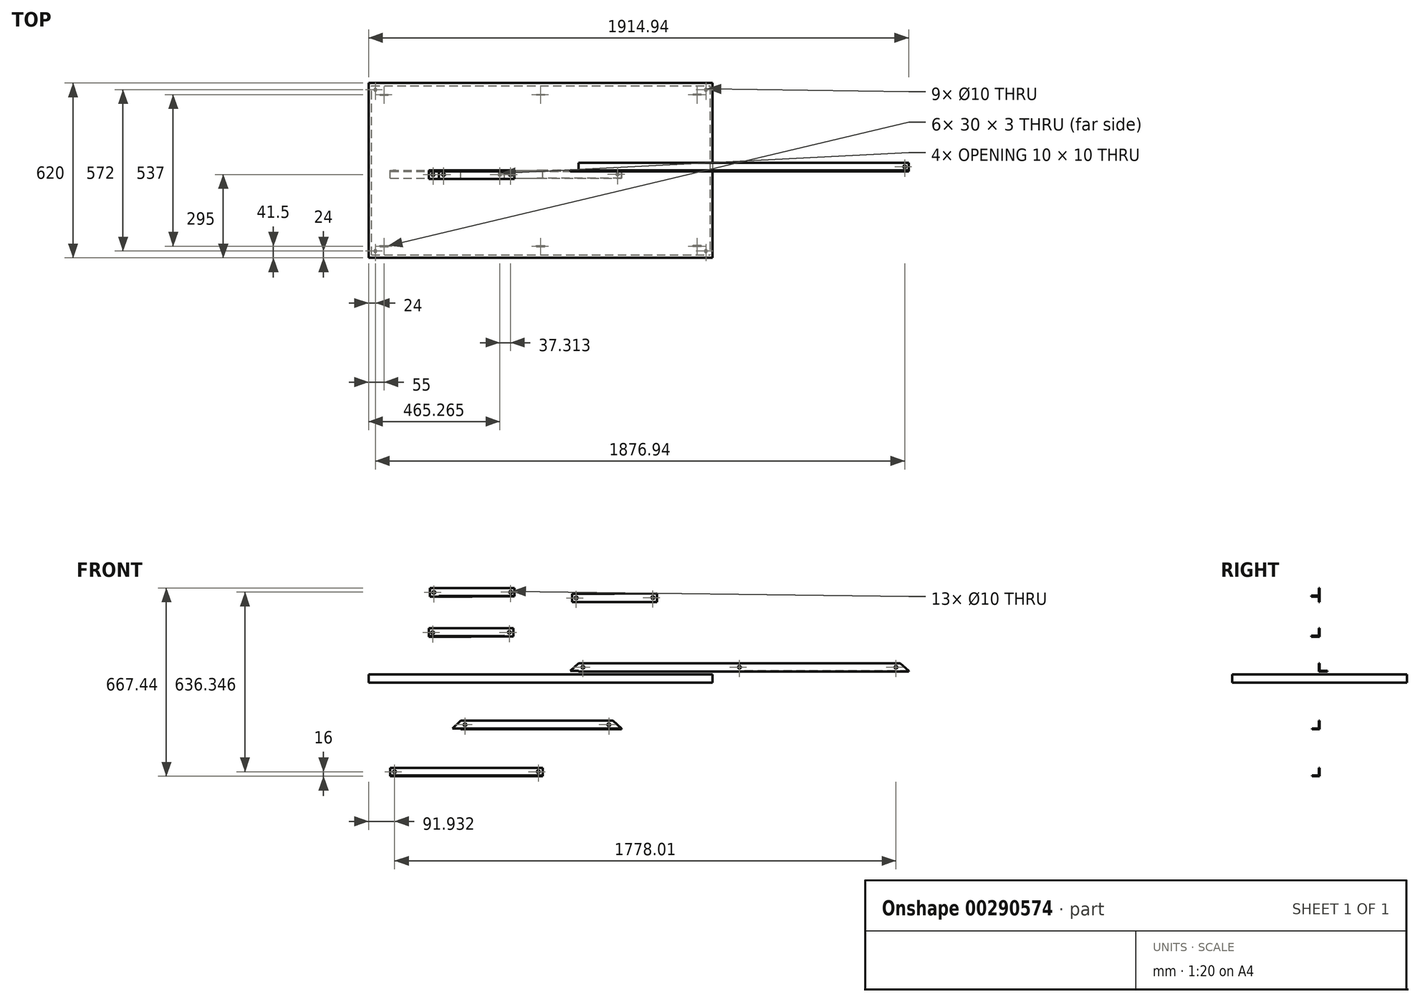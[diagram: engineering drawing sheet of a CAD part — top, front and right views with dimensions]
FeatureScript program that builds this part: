
annotation { "Feature Type Name" : "Feature", "Feature Type Description" : "" }
export const myFeature = defineFeature(function(context is Context, id is Id, definition is map)
    precondition{}
    {
        {
            var Q0;
            Q0=qCreatedBy(makeId("Front.planeOp"),FACE);
            var sketch = newSketch(context, id + "F0", { "sketchPlane" : qUnion([Q0])});
            skLineSegment(sketch, "E0.bottom", {"start": v(104.94, 39.43) * mm, "end": v(704.94, 39.43) * mm});
            skLineSegment(sketch, "E0.top", {"start": v(104.94, 42.43) * mm, "end": v(704.94, 42.43) * mm});
            skLineSegment(sketch, "E0.left", {"start": v(104.94, 39.43) * mm, "end": v(104.94, 42.43) * mm});
            skLineSegment(sketch, "E1.bottom", {"start": v(134.94, 69.43) * mm, "end": v(704.94, 69.43) * mm});
            skLineSegment(sketch, "E1.top", {"start": v(134.94, 42.43) * mm, "end": v(704.94, 42.43) * mm});
            skLineSegment(sketch, "E1.right", {"start": v(704.94, 69.43) * mm, "end": v(704.94, 42.43) * mm});
            skLineSegment(sketch, "E2", {"start": v(134.94, 69.43) * mm, "end": v(104.94, 42.43) * mm});
            skLineSegment(sketch, "E3", {"start": v(134.94, 42.43) * mm, "end": v(134.94, 39.43) * mm});
            skLineSegment(sketch, "E4", {"start": v(704.94, 42.43) * mm, "end": v(704.94, 39.43) * mm});
            skLineSegment(sketch, "E5.MirrorCS", {"start": v(1304.94, 42.43) * mm, "end": v(704.94, 42.43) * mm});
            skLineSegment(sketch, "E6.MirrorCS", {"start": v(1274.94, 69.43) * mm, "end": v(1304.94, 42.43) * mm});
            skLineSegment(sketch, "E7.MirrorCS", {"start": v(1274.94, 69.43) * mm, "end": v(704.94, 69.43) * mm});
            skLineSegment(sketch, "E8.MirrorCS", {"start": v(1274.94, 42.43) * mm, "end": v(1274.94, 39.43) * mm});
            skLineSegment(sketch, "E9.MirrorCS", {"start": v(1304.94, 39.43) * mm, "end": v(1304.94, 42.43) * mm});
            skLineSegment(sketch, "E10", {"start": v(704.94, 39.43) * mm, "end": v(1304.94, 39.43) * mm});
            skLineSegment(sketch, "E11", {"start": v(134.94, 69.43) * mm, "end": v(134.94, 42.43) * mm});
            skLineSegment(sketch, "E12", {"start": v(149.94, 69.43) * mm, "end": v(149.94, 42.43) * mm});
            skPoint(sketch, "E13", {"position": v(149.94, 55.43) * mm});
            skPoint(sketch, "E14", {"position": v(704.94, 55.43) * mm});
            skLineSegment(sketch, "E15.MirrorCS", {"start": v(1259.94, 69.43) * mm, "end": v(1259.94, 42.43) * mm});
            skPoint(sketch, "E16.MirrorP", {"position": v(1259.94, 55.43) * mm});
            skLineSegment(sketch, "E17.MirrorCS", {"start": v(1274.94, 69.43) * mm, "end": v(1274.94, 42.43) * mm});
            skCircle(sketch, "E18", {"center": v(704.94, 55.43) * mm, "radius": 5 * mm});
            skCircle(sketch, "E19", {"center": v(149.94, 55.43) * mm, "radius": 5 * mm});
            skCircle(sketch, "E20.MirrorC", {"center": v(1259.94, 55.43) * mm, "radius": 5 * mm});
            skLineSegment(sketch, "E21.bottom", {"start": v(-313.14, -164.51) * mm, "end": v(-13.14, -164.51) * mm});
            skLineSegment(sketch, "E21.top", {"start": v(-313.14, -161.51) * mm, "end": v(-13.14, -161.51) * mm});
            skLineSegment(sketch, "E21.left", {"start": v(-313.14, -164.51) * mm, "end": v(-313.14, -161.51) * mm});
            skLineSegment(sketch, "E22.bottom", {"start": v(-283.14, -134.51) * mm, "end": v(-13.14, -134.51) * mm});
            skLineSegment(sketch, "E22.top", {"start": v(-283.14, -161.51) * mm, "end": v(-13.14, -161.51) * mm});
            skLineSegment(sketch, "E22.right", {"start": v(-13.14, -134.51) * mm, "end": v(-13.14, -161.51) * mm});
            skLineSegment(sketch, "E23", {"start": v(-283.14, -134.51) * mm, "end": v(-313.14, -161.51) * mm});
            skLineSegment(sketch, "E24", {"start": v(-283.14, -161.51) * mm, "end": v(-283.14, -164.51) * mm});
            skLineSegment(sketch, "E25", {"start": v(-13.14, -161.51) * mm, "end": v(-13.14, -164.51) * mm});
            skLineSegment(sketch, "E26.MirrorCS", {"start": v(286.86, -161.51) * mm, "end": v(-13.14, -161.51) * mm});
            skLineSegment(sketch, "E27.MirrorCS", {"start": v(256.86, -134.51) * mm, "end": v(286.86, -161.51) * mm});
            skLineSegment(sketch, "E28.MirrorCS", {"start": v(256.86, -134.51) * mm, "end": v(-13.14, -134.51) * mm});
            skLineSegment(sketch, "E29.MirrorCS", {"start": v(256.86, -161.51) * mm, "end": v(256.86, -164.51) * mm});
            skLineSegment(sketch, "E30.MirrorCS", {"start": v(286.86, -164.51) * mm, "end": v(286.86, -161.51) * mm});
            skLineSegment(sketch, "E31", {"start": v(-13.14, -164.51) * mm, "end": v(286.86, -164.51) * mm});
            skLineSegment(sketch, "E32", {"start": v(-283.14, -134.51) * mm, "end": v(-283.14, -161.51) * mm});
            skLineSegment(sketch, "E33", {"start": v(-268.14, -134.51) * mm, "end": v(-268.14, -161.51) * mm});
            skPoint(sketch, "E34", {"position": v(-268.14, -148.51) * mm});
            skPoint(sketch, "E35", {"position": v(-13.14, -148.51) * mm});
            skLineSegment(sketch, "E36.MirrorCS", {"start": v(241.86, -134.51) * mm, "end": v(241.86, -161.51) * mm});
            skPoint(sketch, "E37.MirrorP", {"position": v(241.86, -148.51) * mm});
            skLineSegment(sketch, "E38.MirrorCS", {"start": v(256.86, -134.51) * mm, "end": v(256.86, -161.51) * mm});
            skCircle(sketch, "E39", {"center": v(-268.14, -148.51) * mm, "radius": 5 * mm});
            skCircle(sketch, "E40.MirrorC", {"center": v(241.86, -148.51) * mm, "radius": 5 * mm});
            skLineSegment(sketch, "E41.bottom", {"start": v(-396.7, 163.02) * mm, "end": v(-246.72, 163.02) * mm});
            skLineSegment(sketch, "E41.top", {"start": v(-396.7, 166.02) * mm, "end": v(-246.72, 166.02) * mm});
            skLineSegment(sketch, "E42.bottom", {"start": v(-396.9, 193.02) * mm, "end": v(-246.81, 193.02) * mm});
            skLineSegment(sketch, "E42.right", {"start": v(-246.81, 193.02) * mm, "end": v(-246.72, 166.02) * mm});
            skLineSegment(sketch, "E43", {"start": v(-396.7, 166.02) * mm, "end": v(-396.7, 163.02) * mm});
            skLineSegment(sketch, "E44", {"start": v(-246.72, 166.02) * mm, "end": v(-246.72, 163.02) * mm});
            skLineSegment(sketch, "E45.MirrorCS", {"start": v(-96.74, 167.05) * mm, "end": v(-246.72, 166.02) * mm});
            skLineSegment(sketch, "E46.MirrorCS", {"start": v(-96.74, 194.05) * mm, "end": v(-246.81, 193.02) * mm});
            skLineSegment(sketch, "E47.MirrorCS", {"start": v(-96.74, 167.05) * mm, "end": v(-96.71, 164.05) * mm});
            skLineSegment(sketch, "E48", {"start": v(-246.72, 163.02) * mm, "end": v(-96.71, 164.05) * mm});
            skLineSegment(sketch, "E49", {"start": v(-396.9, 193.02) * mm, "end": v(-396.7, 166.02) * mm});
            skLineSegment(sketch, "E50.MirrorCS", {"start": v(-96.74, 194.05) * mm, "end": v(-96.74, 167.05) * mm});
            skCircle(sketch, "E51", {"center": v(-382.8, 178.02) * mm, "radius": 5 * mm});
            skPoint(sketch, "E52.MirrorCS.start.orphan", {"position": v(-96.74, 194.05) * mm});
            skCircle(sketch, "E53.MirrorC", {"center": v(-110.74, 178.95) * mm, "radius": 5 * mm});
            skLineSegment(sketch, "E54.bottom", {"start": v(-533.07, -331.09) * mm, "end": v(-263.07, -331.09) * mm});
            skLineSegment(sketch, "E54.top", {"start": v(-533.07, -328.09) * mm, "end": v(-263.07, -328.09) * mm});
            skLineSegment(sketch, "E55.bottom", {"start": v(-533.07, -301.09) * mm, "end": v(-263.07, -301.09) * mm});
            skLineSegment(sketch, "E55.right", {"start": v(-263.07, -301.09) * mm, "end": v(-263.07, -328.09) * mm});
            skLineSegment(sketch, "E56", {"start": v(-533.07, -328.09) * mm, "end": v(-533.07, -331.09) * mm});
            skLineSegment(sketch, "E57", {"start": v(-263.07, -328.09) * mm, "end": v(-263.07, -331.09) * mm});
            skLineSegment(sketch, "E58.MirrorCS", {"start": v(6.93, -328.09) * mm, "end": v(-263.07, -328.09) * mm});
            skLineSegment(sketch, "E59.MirrorCS", {"start": v(6.93, -301.09) * mm, "end": v(-263.07, -301.09) * mm});
            skLineSegment(sketch, "E60.MirrorCS", {"start": v(6.93, -328.09) * mm, "end": v(6.93, -331.09) * mm});
            skLineSegment(sketch, "E61", {"start": v(-263.07, -331.09) * mm, "end": v(6.93, -331.09) * mm});
            skLineSegment(sketch, "E62", {"start": v(-533.07, -301.09) * mm, "end": v(-533.07, -328.09) * mm});
            skLineSegment(sketch, "E63", {"start": v(-518.07, -301.09) * mm, "end": v(-518.07, -328.09) * mm});
            skPoint(sketch, "E64", {"position": v(-518.07, -315.09) * mm});
            skPoint(sketch, "E65", {"position": v(-263.07, -315.09) * mm});
            skLineSegment(sketch, "E66.MirrorCS", {"start": v(-8.07, -301.09) * mm, "end": v(-8.07, -328.09) * mm});
            skPoint(sketch, "E67.MirrorP", {"position": v(-8.07, -315.09) * mm});
            skLineSegment(sketch, "E68.MirrorCS", {"start": v(6.93, -301.09) * mm, "end": v(6.93, -328.09) * mm});
            skCircle(sketch, "E69", {"center": v(-518.07, -315.09) * mm, "radius": 5 * mm});
            skCircle(sketch, "E70.MirrorC", {"center": v(-8.07, -315.09) * mm, "radius": 5 * mm});
            skLineSegment(sketch, "E71.bottom", {"start": v(112, 285.9) * mm, "end": v(261.99, 285.9) * mm});
            skLineSegment(sketch, "E72.bottom", {"start": v(111.81, 315.9) * mm, "end": v(261.9, 315.9) * mm});
            skLineSegment(sketch, "E73", {"start": v(112, 288.9) * mm, "end": v(112, 285.9) * mm});
            skLineSegment(sketch, "E74", {"start": v(261.99, 288.9) * mm, "end": v(261.99, 285.9) * mm});
            skLineSegment(sketch, "E75.MirrorCS", {"start": v(411.97, 316.93) * mm, "end": v(261.9, 315.9) * mm});
            skLineSegment(sketch, "E76.MirrorCS", {"start": v(411.97, 289.93) * mm, "end": v(412, 286.93) * mm});
            skLineSegment(sketch, "E77", {"start": v(261.99, 285.9) * mm, "end": v(412, 286.93) * mm});
            skLineSegment(sketch, "E78", {"start": v(111.81, 315.9) * mm, "end": v(112, 288.9) * mm});
            skLineSegment(sketch, "E79.MirrorCS", {"start": v(411.97, 316.93) * mm, "end": v(411.97, 289.93) * mm});
            skCircle(sketch, "E80", {"center": v(125.92, 300.9) * mm, "radius": 5 * mm});
            skPoint(sketch, "E81.MirrorCS.start.orphan", {"position": v(411.97, 316.93) * mm});
            skCircle(sketch, "E82.MirrorC", {"center": v(397.97, 301.84) * mm, "radius": 5 * mm});
            skLineSegment(sketch, "E83.bottom", {"start": v(-392.4, 305.32) * mm, "end": v(-242.4, 305.32) * mm});
            skLineSegment(sketch, "E83.top", {"start": v(-392.4, 308.32) * mm, "end": v(-242.4, 308.32) * mm});
            skLineSegment(sketch, "E84.bottom", {"start": v(-392.58, 335.32) * mm, "end": v(-242.5, 335.32) * mm});
            skLineSegment(sketch, "E84.right", {"start": v(-242.5, 335.32) * mm, "end": v(-242.4, 308.32) * mm});
            skLineSegment(sketch, "E85", {"start": v(-392.4, 308.32) * mm, "end": v(-392.4, 305.32) * mm});
            skLineSegment(sketch, "E86", {"start": v(-242.4, 308.32) * mm, "end": v(-242.4, 305.32) * mm});
            skLineSegment(sketch, "E87.MirrorCS", {"start": v(-92.42, 309.35) * mm, "end": v(-242.4, 308.32) * mm});
            skLineSegment(sketch, "E88.MirrorCS", {"start": v(-92.42, 336.35) * mm, "end": v(-242.5, 335.32) * mm});
            skLineSegment(sketch, "E89.MirrorCS", {"start": v(-92.42, 309.35) * mm, "end": v(-92.4, 306.35) * mm});
            skLineSegment(sketch, "E90", {"start": v(-242.4, 305.32) * mm, "end": v(-92.4, 306.35) * mm});
            skLineSegment(sketch, "E91", {"start": v(-392.58, 335.32) * mm, "end": v(-392.4, 308.32) * mm});
            skLineSegment(sketch, "E92.MirrorCS", {"start": v(-92.42, 336.35) * mm, "end": v(-92.42, 309.35) * mm});
            skCircle(sketch, "E93", {"center": v(-378.48, 320.32) * mm, "radius": 5 * mm});
            skPoint(sketch, "E94.MirrorCS.start.orphan", {"position": v(-92.42, 336.35) * mm});
            skCircle(sketch, "E95.MirrorC", {"center": v(-106.42, 321.26) * mm, "radius": 5 * mm});
            skLineSegment(sketch, "E96", {"start": v(-360.4, 308.32) * mm, "end": v(-360.4, 305.32) * mm});
            skLineSegment(sketch, "E97", {"start": v(-128.74, 166.83) * mm, "end": v(-128.71, 163.83) * mm});
            skSolve(sketch);
        }
        {
            var Q0;
            Q0=makeQuery(id+"F0.imprint","IMPRINT",FACE,{"disambiguationData":[TD([[makeQuery(id+"F0.imprint","IMPRINT",EDGE,{"derivedFrom":sQuery(id+"F0.wireOp",EDGE,"E1.top")}),-1.0]])]});
            var Q1;
            Q1=makeQuery(id+"F0.imprint","IMPRINT",FACE,{"disambiguationData":[TD([[makeQuery(id+"F0.imprint","IMPRINT",EDGE,{"derivedFrom":sQuery(id+"F0.wireOp",EDGE,"E0.top")}),-1.0]])]});
            var Q2;
            {var subQ0=sQuery(id+"F0.wireOp",EDGE,"E4");Q2=makeQuery(id+"F0.imprint","IMPRINT",FACE,{"disambiguationData":[TD([[makeQuery(id+"F0.imprint","IMPRINT",EDGE,{"derivedFrom":subQ0}),1.0]])]});}
            var Q3;
            {var subQ2=sQuery(id+"F0.wireOp",EDGE,"E8.MirrorCS");Q3=makeQuery(id+"F0.imprint","IMPRINT",FACE,{"disambiguationData":[TD([[makeQuery(id+"F0.imprint","IMPRINT",EDGE,{"derivedFrom":subQ2}),1.0]])]});}
            extrude(context, id + "F1", {"entities" : qUnion([Q0, Q1, Q2, Q3]), "oppositeDirection" : true, "depth" : 27 * mm});
        }
        {
            var Q0;
            Q0=makeQuery(id+"F0.imprint","IMPRINT",FACE,{"disambiguationData":[TD([[makeQuery(id+"F0.imprint","IMPRINT",EDGE,{"derivedFrom":sQuery(id+"F0.wireOp",EDGE,"E0.top")}),-1.0]])]});
            var Q1;
            Q1=makeQuery(id+"F0.imprint","IMPRINT",FACE,{"disambiguationData":[TD([[makeQuery(id+"F0.imprint","IMPRINT",EDGE,{"derivedFrom":sQuery(id+"F0.wireOp",EDGE,"E0.top")}),1.0]])]});
            var Q2;
            {var subQ0=sQuery(id+"F0.wireOp",EDGE,"E6.MirrorCS");Q2=makeQuery(id+"F0.imprint","IMPRINT",FACE,{"disambiguationData":[TD([[makeQuery(id+"F0.imprint","IMPRINT",EDGE,{"derivedFrom":subQ0}),-1.0]])]});}
            var Q3;
            {var subQ2=sQuery(id+"F0.wireOp",EDGE,"E8.MirrorCS");Q3=makeQuery(id+"F0.imprint","IMPRINT",FACE,{"disambiguationData":[TD([[makeQuery(id+"F0.imprint","IMPRINT",EDGE,{"derivedFrom":subQ2}),1.0]])]});}
            var Q4;
            Q4=makeQuery(id+"F0.imprint","IMPRINT",FACE,{"disambiguationData":[TD([[makeQuery(id+"F0.imprint","IMPRINT",EDGE,{"derivedFrom":sQuery(id+"F0.wireOp",EDGE,"E21.top")}),-1.0]])]});
            var Q5;
            Q5=makeQuery(id+"F0.imprint","IMPRINT",FACE,{"disambiguationData":[TD([[makeQuery(id+"F0.imprint","IMPRINT",EDGE,{"derivedFrom":sQuery(id+"F0.wireOp",EDGE,"E21.top")}),1.0]])]});
            var Q6;
            {var subQ0=sQuery(id+"F0.wireOp",EDGE,"E27.MirrorCS");Q6=makeQuery(id+"F0.imprint","IMPRINT",FACE,{"disambiguationData":[TD([[makeQuery(id+"F0.imprint","IMPRINT",EDGE,{"derivedFrom":subQ0}),-1.0]])]});}
            var Q7;
            {var subQ2=sQuery(id+"F0.wireOp",EDGE,"E29.MirrorCS");Q7=makeQuery(id+"F0.imprint","IMPRINT",FACE,{"disambiguationData":[TD([[makeQuery(id+"F0.imprint","IMPRINT",EDGE,{"derivedFrom":subQ2}),1.0]])]});}
            var Q8;
            Q8=makeQuery(id+"F0.imprint","IMPRINT",FACE,{"disambiguationData":[TD([[makeQuery(id+"F0.imprint","IMPRINT",EDGE,{"derivedFrom":sQuery(id+"F0.wireOp",EDGE,"E41.bottom")}),1.0]])]});
            var Q9;
            Q9=makeQuery(id+"F0.imprint","IMPRINT",FACE,{"disambiguationData":[TD([[makeQuery(id+"F0.imprint","IMPRINT",EDGE,{"derivedFrom":sQuery(id+"F0.wireOp",EDGE,"E44")}),1.0]])]});
            var Q10;
            Q10=makeQuery(id+"F0.imprint","IMPRINT",FACE,{"disambiguationData":[TD([[makeQuery(id+"F0.imprint","IMPRINT",EDGE,{"derivedFrom":sQuery(id+"F0.wireOp",EDGE,"E71.bottom")}),1.0]])]});
            var Q11;
            Q11=makeQuery(id+"F0.imprint","IMPRINT",FACE,{"disambiguationData":[TD([[makeQuery(id+"F0.imprint","IMPRINT",EDGE,{"derivedFrom":sQuery(id+"F0.wireOp",EDGE,"E42.bottom")}),-1.0]])]});
            var Q12;
            Q12=makeQuery(id+"F0.imprint","IMPRINT",FACE,{"disambiguationData":[TD([[makeQuery(id+"F0.imprint","IMPRINT",EDGE,{"derivedFrom":sQuery(id+"F0.wireOp",EDGE,"E42.right")}),1.0]])]});
            var Q13;
            Q13=makeQuery(id+"F0.imprint","IMPRINT",FACE,{"disambiguationData":[TD([[makeQuery(id+"F0.imprint","IMPRINT",EDGE,{"derivedFrom":sQuery(id+"F0.wireOp",EDGE,"E54.bottom")}),1.0]])]});
            var Q14;
            {var subQ5=sQuery(id+"F0.wireOp",EDGE,"E62");Q14=makeQuery(id+"F0.imprint","IMPRINT",FACE,{"disambiguationData":[TD([[makeQuery(id+"F0.imprint","IMPRINT",EDGE,{"derivedFrom":subQ5}),1.0]])]});}
            var Q15;
            {var subQ1=sQuery(id+"F0.wireOp",EDGE,"E57");Q15=makeQuery(id+"F0.imprint","IMPRINT",FACE,{"disambiguationData":[TD([[makeQuery(id+"F0.imprint","IMPRINT",EDGE,{"derivedFrom":subQ1}),1.0]])]});}
            var Q16;
            {var subQ5=sQuery(id+"F0.wireOp",EDGE,"E68.MirrorCS");Q16=makeQuery(id+"F0.imprint","IMPRINT",FACE,{"disambiguationData":[TD([[makeQuery(id+"F0.imprint","IMPRINT",EDGE,{"derivedFrom":subQ5}),-1.0]])]});}
            var Q17;
            {var subQ0=sQuery(id+"F0.wireOp",EDGE,"E3");Q17=makeQuery(id+"F0.imprint","IMPRINT",FACE,{"disambiguationData":[TD([[makeQuery(id+"F0.imprint","IMPRINT",EDGE,{"derivedFrom":subQ0}),1.0]])]});}
            var Q18;
            {var subQ5=sQuery(id+"F0.wireOp",EDGE,"E11");Q18=makeQuery(id+"F0.imprint","IMPRINT",FACE,{"disambiguationData":[TD([[makeQuery(id+"F0.imprint","IMPRINT",EDGE,{"derivedFrom":subQ5}),1.0]])]});}
            var Q19;
            {var subQ1=sQuery(id+"F0.wireOp",EDGE,"E4");Q19=makeQuery(id+"F0.imprint","IMPRINT",FACE,{"disambiguationData":[TD([[makeQuery(id+"F0.imprint","IMPRINT",EDGE,{"derivedFrom":subQ1}),1.0]])]});}
            var Q20;
            {var subQ5=sQuery(id+"F0.wireOp",EDGE,"E17.MirrorCS");Q20=makeQuery(id+"F0.imprint","IMPRINT",FACE,{"disambiguationData":[TD([[makeQuery(id+"F0.imprint","IMPRINT",EDGE,{"derivedFrom":subQ5}),-1.0]])]});}
            var Q21;
            {var subQ0=sQuery(id+"F0.wireOp",EDGE,"E24");Q21=makeQuery(id+"F0.imprint","IMPRINT",FACE,{"disambiguationData":[TD([[makeQuery(id+"F0.imprint","IMPRINT",EDGE,{"derivedFrom":subQ0}),1.0]])]});}
            var Q22;
            {var subQ5=sQuery(id+"F0.wireOp",EDGE,"E32");Q22=makeQuery(id+"F0.imprint","IMPRINT",FACE,{"disambiguationData":[TD([[makeQuery(id+"F0.imprint","IMPRINT",EDGE,{"derivedFrom":subQ5}),1.0]])]});}
            var Q23;
            {var subQ1=sQuery(id+"F0.wireOp",EDGE,"E25");Q23=makeQuery(id+"F0.imprint","IMPRINT",FACE,{"disambiguationData":[TD([[makeQuery(id+"F0.imprint","IMPRINT",EDGE,{"derivedFrom":subQ1}),1.0]])]});}
            var Q24;
            {var subQ5=sQuery(id+"F0.wireOp",EDGE,"E38.MirrorCS");Q24=makeQuery(id+"F0.imprint","IMPRINT",FACE,{"disambiguationData":[TD([[makeQuery(id+"F0.imprint","IMPRINT",EDGE,{"derivedFrom":subQ5}),-1.0]])]});}
            var Q25;
            {var subQ1=sQuery(id+"F0.wireOp",EDGE,"E1.bottom");var subQ7=sQuery(id+"F0.wireOp",EDGE,"E12");var subQ10=makeQuery(id+"F0.imprint","INTERSECT",VERTEX,{"derivedFrom":[subQ1,subQ7]});Q25=makeQuery(id+"F0.imprint","IMPRINT",FACE,{"disambiguationData":[TD([[makeQuery(id+"F0.imprint","IMPRINT",EDGE,{"disambiguationData":[TD([[subQ10,-1.0]])],"derivedFrom":subQ7}),1.0]])]});}
            var Q26;
            {var subQ0=sQuery(id+"F0.wireOp",EDGE,"E7.MirrorCS");var subQ3=sQuery(id+"F0.wireOp",EDGE,"E15.MirrorCS");var subQ4=makeQuery(id+"F0.imprint","INTERSECT",VERTEX,{"derivedFrom":[subQ0,subQ3]});Q26=makeQuery(id+"F0.imprint","IMPRINT",FACE,{"disambiguationData":[TD([[makeQuery(id+"F0.imprint","IMPRINT",EDGE,{"disambiguationData":[TD([[subQ4,-1.0]])],"derivedFrom":subQ3}),-1.0]])]});}
            var Q27;
            {var subQ1=sQuery(id+"F0.wireOp",EDGE,"E22.bottom");var subQ7=sQuery(id+"F0.wireOp",EDGE,"E33");var subQ10=makeQuery(id+"F0.imprint","INTERSECT",VERTEX,{"derivedFrom":[subQ1,subQ7]});Q27=makeQuery(id+"F0.imprint","IMPRINT",FACE,{"disambiguationData":[TD([[makeQuery(id+"F0.imprint","IMPRINT",EDGE,{"disambiguationData":[TD([[subQ10,-1.0]])],"derivedFrom":subQ7}),1.0]])]});}
            var Q28;
            {var subQ1=sQuery(id+"F0.wireOp",EDGE,"E55.bottom");var subQ6=sQuery(id+"F0.wireOp",EDGE,"E63");var subQ13=makeQuery(id+"F0.imprint","INTERSECT",VERTEX,{"derivedFrom":[subQ1,subQ6]});Q28=makeQuery(id+"F0.imprint","IMPRINT",FACE,{"disambiguationData":[TD([[makeQuery(id+"F0.imprint","IMPRINT",EDGE,{"disambiguationData":[TD([[subQ13,-1.0]])],"derivedFrom":subQ6}),1.0]])]});}
            var Q29;
            {var subQ0=sQuery(id+"F0.wireOp",EDGE,"E59.MirrorCS");var subQ3=sQuery(id+"F0.wireOp",EDGE,"E66.MirrorCS");var subQ4=makeQuery(id+"F0.imprint","INTERSECT",VERTEX,{"derivedFrom":[subQ0,subQ3]});Q29=makeQuery(id+"F0.imprint","IMPRINT",FACE,{"disambiguationData":[TD([[makeQuery(id+"F0.imprint","IMPRINT",EDGE,{"disambiguationData":[TD([[subQ4,-1.0]])],"derivedFrom":subQ3}),-1.0]])]});}
            var Q30;
            {var subQ0=sQuery(id+"F0.wireOp",EDGE,"a2b34186-37aa-447c-9af8-30680829358e");var subQ1=sQuery(id+"F0.wireOp",EDGE,"E22.right");var subQ2=makeQuery(id+"F0.imprint","INTERSECT",VERTEX,{"disambiguationData":[OD(0.0)],"derivedFrom":[subQ1,subQ0]});Q30=makeQuery(id+"F0.imprint","IMPRINT",FACE,{"disambiguationData":[TD([[makeQuery(id+"F0.imprint","IMPRINT",EDGE,{"disambiguationData":[TD([[subQ2,-1.0]])],"derivedFrom":subQ1}),1.0]])]});}
            var Q31;
            {var subQ0=sQuery(id+"F0.wireOp",EDGE,"a2b34186-37aa-447c-9af8-30680829358e");var subQ1=sQuery(id+"F0.wireOp",EDGE,"E22.right");var subQ2=makeQuery(id+"F0.imprint","INTERSECT",VERTEX,{"disambiguationData":[OD(0.0)],"derivedFrom":[subQ1,subQ0]});Q31=makeQuery(id+"F0.imprint","IMPRINT",FACE,{"disambiguationData":[TD([[makeQuery(id+"F0.imprint","IMPRINT",EDGE,{"disambiguationData":[TD([[subQ2,-1.0]])],"derivedFrom":subQ1}),-1.0]])]});}
            var Q32;
            Q32=makeQuery(id+"F0.imprint","IMPRINT",FACE,{"disambiguationData":[TD([[makeQuery(id+"F0.imprint","IMPRINT",EDGE,{"derivedFrom":sQuery(id+"F0.wireOp",EDGE,"E84.bottom")}),-1.0]])]});
            var Q33;
            Q33=makeQuery(id+"F0.imprint","IMPRINT",FACE,{"disambiguationData":[TD([[makeQuery(id+"F0.imprint","IMPRINT",EDGE,{"derivedFrom":sQuery(id+"F0.wireOp",EDGE,"E84.right")}),1.0]])]});
            var Q34;
            Q34=makeQuery(id+"F0.imprint","IMPRINT",FACE,{"disambiguationData":[TD([[makeQuery(id+"F0.imprint","IMPRINT",EDGE,{"derivedFrom":sQuery(id+"F0.wireOp",EDGE,"E83.bottom")}),1.0]])]});
            var Q35;
            Q35=makeQuery(id+"F0.imprint","IMPRINT",FACE,{"disambiguationData":[TD([[makeQuery(id+"F0.imprint","IMPRINT",EDGE,{"derivedFrom":sQuery(id+"F0.wireOp",EDGE,"E86")}),1.0]])]});
            var Q36;
            {var subQ0=sQuery(id+"F0.wireOp",EDGE,"E47.MirrorCS");Q36=makeQuery(id+"F0.imprint","IMPRINT",FACE,{"disambiguationData":[TD([[makeQuery(id+"F0.imprint","IMPRINT",EDGE,{"derivedFrom":subQ0}),-1.0]])]});}
            extrude(context, id + "F2", {"entities" : qUnion([Q0, Q1, Q2, Q3, Q4, Q5, Q6, Q7, Q8, Q9, Q10, Q11, Q12, Q13, Q14, Q15, Q16, Q17, Q18, Q19, Q20, Q21, Q22, Q23, Q24, Q25, Q26, Q27, Q28, Q29, Q30, Q31, Q32, Q33, Q34, Q35, Q36]), "operationType" : NewBodyOperationType.ADD, "depth" : 3 * mm});
        }
        {
            var Q0;
            Q0=makeQuery(id+"F1.opExtrude","SWEPT_FACE",FACE,{"disambiguationData":[OSD([sQuery(id+"F0.wireOp",EDGE,"E0.top"),sQuery(id+"F0.wireOp",EDGE,"E1.top")])]});
            var sketch = newSketch(context, id + "F3", { "sketchPlane" : qUnion([Q0])});
            skLineSegment(sketch, "E98", {"start": v(118.94, 27) * mm, "end": v(118.94, 0) * mm});
            skPoint(sketch, "E99", {"position": v(118.94, 13) * mm});
            skCircle(sketch, "E100", {"center": v(118.94, 13) * mm, "radius": 5 * mm});
            skLineSegment(sketch, "E101.MirrorCS", {"start": v(1290.94, 27) * mm, "end": v(1290.94, 0) * mm});
            skPoint(sketch, "E102.MirrorP", {"position": v(1290.94, 13) * mm});
            skCircle(sketch, "E103.MirrorC", {"center": v(1290.94, 13) * mm, "radius": 5 * mm});
            skLineSegment(sketch, "E104", {"start": v(104.94, 27) * mm, "end": v(104.94, 0) * mm});
            skSolve(sketch);
        }
        {
            var Q0;
            Q0 = qSketchRegion(id + "F3", true);
            extrude(context, id + "F4", {"entities" : qUnion([Q0]), "operationType" : NewBodyOperationType.REMOVE, "endBound" : BoundingType.THROUGH_ALL, "oppositeDirection" : true, "depth" : 25 * mm});
        }
        {
            var Q0;
            Q0=qCreatedBy(makeId("Top.planeOp"),FACE);
            var sketch = newSketch(context, id + "F5", { "sketchPlane" : qUnion([Q0])});
            skLineSegment(sketch, "E105.bottom", {"start": v(-600, 270) * mm, "end": v(0, 270) * mm});
            skLineSegment(sketch, "E105.top", {"start": v(-600, 300) * mm, "end": v(0, 300) * mm});
            skLineSegment(sketch, "E105.left", {"start": v(-600, 270) * mm, "end": v(-600, 300) * mm});
            skLineSegment(sketch, "E105.right", {"start": v(0, 270) * mm, "end": v(0, 300) * mm});
            skLineSegment(sketch, "E106.bottom", {"start": v(-600, 300) * mm, "end": v(-570, 300) * mm});
            skLineSegment(sketch, "E106.top", {"start": v(-600, 0) * mm, "end": v(-570, 0) * mm});
            skLineSegment(sketch, "E106.left", {"start": v(-600, 300) * mm, "end": v(-600, 0) * mm});
            skLineSegment(sketch, "E106.right", {"start": v(-570, 300) * mm, "end": v(-570, 0) * mm});
            skLineSegment(sketch, "E107.bottom", {"start": v(-570, 270) * mm, "end": v(-540, 270) * mm});
            skLineSegment(sketch, "E107.top", {"start": v(-570, 267) * mm, "end": v(-540, 267) * mm});
            skLineSegment(sketch, "E107.left", {"start": v(-570, 270) * mm, "end": v(-570, 267) * mm});
            skLineSegment(sketch, "E107.right", {"start": v(-540, 270) * mm, "end": v(-540, 267) * mm});
            skLineSegment(sketch, "E108.bottom", {"start": v(-570, 267) * mm, "end": v(-567, 267) * mm});
            skLineSegment(sketch, "E108.left", {"start": v(-570, 267) * mm, "end": v(-570, 240) * mm});
            skLineSegment(sketch, "E109.bottom", {"start": v(-15, 270) * mm, "end": v(0, 270) * mm});
            skLineSegment(sketch, "E109.top", {"start": v(-15, 267) * mm, "end": v(0, 267) * mm});
            skLineSegment(sketch, "E109.left", {"start": v(-15, 270) * mm, "end": v(-15, 267) * mm});
            skLineSegment(sketch, "E109.right", {"start": v(0, 270) * mm, "end": v(0, 267) * mm});
            skLineSegment(sketch, "E110.MirrorCS", {"start": v(600, 300) * mm, "end": v(0, 300) * mm});
            skLineSegment(sketch, "E111.MirrorCS", {"start": v(600, 300) * mm, "end": v(600, 0) * mm});
            skLineSegment(sketch, "E112.MirrorCS", {"start": v(600, 270) * mm, "end": v(0, 270) * mm});
            skLineSegment(sketch, "E113.MirrorCS", {"start": v(570, 300) * mm, "end": v(570, 0) * mm});
            skLineSegment(sketch, "E114.MirrorCS", {"start": v(570, 267) * mm, "end": v(540, 267) * mm});
            skLineSegment(sketch, "E115.MirrorCS", {"start": v(540, 270) * mm, "end": v(540, 267) * mm});
            skLineSegment(sketch, "E116.MirrorCS", {"start": v(15, 267) * mm, "end": v(0, 267) * mm});
            skLineSegment(sketch, "E117.MirrorCS", {"start": v(15, 270) * mm, "end": v(15, 267) * mm});
            skLineSegment(sketch, "E118.MirrorCS", {"start": v(600, 0) * mm, "end": v(570, 0) * mm});
            skLineSegment(sketch, "E119.MirrorCS", {"start": v(0, -270) * mm, "end": v(0, -267) * mm});
            skLineSegment(sketch, "E120.MirrorCS", {"start": v(15, -267) * mm, "end": v(0, -267) * mm});
            skLineSegment(sketch, "E121.MirrorCS", {"start": v(-15, -267) * mm, "end": v(0, -267) * mm});
            skLineSegment(sketch, "E122.MirrorCS", {"start": v(-570, -267) * mm, "end": v(-567, -267) * mm});
            skLineSegment(sketch, "E123.MirrorCS", {"start": v(-570, -270) * mm, "end": v(-570, -267) * mm});
            skLineSegment(sketch, "E124.MirrorCS", {"start": v(-15, -270) * mm, "end": v(-15, -267) * mm});
            skLineSegment(sketch, "E125.MirrorCS", {"start": v(-15, -270) * mm, "end": v(0, -270) * mm});
            skLineSegment(sketch, "E126.MirrorCS", {"start": v(-570, -270) * mm, "end": v(-540, -270) * mm});
            skLineSegment(sketch, "E127.MirrorCS", {"start": v(0, -270) * mm, "end": v(0, -300) * mm});
            skLineSegment(sketch, "E128.MirrorCS", {"start": v(-570, -267) * mm, "end": v(-540, -267) * mm});
            skLineSegment(sketch, "E129.MirrorCS", {"start": v(-540, -270) * mm, "end": v(-540, -267) * mm});
            skLineSegment(sketch, "E130.MirrorCS", {"start": v(-570, -267) * mm, "end": v(-570, -240) * mm});
            skLineSegment(sketch, "E131.MirrorCS", {"start": v(-600, -270) * mm, "end": v(-600, -300) * mm});
            skLineSegment(sketch, "E132.MirrorCS", {"start": v(15, -270) * mm, "end": v(15, -267) * mm});
            skLineSegment(sketch, "E133.MirrorCS", {"start": v(540, -270) * mm, "end": v(540, -267) * mm});
            skLineSegment(sketch, "E134.MirrorCS", {"start": v(570, -267) * mm, "end": v(540, -267) * mm});
            skLineSegment(sketch, "E135.MirrorCS", {"start": v(-600, -300) * mm, "end": v(-570, -300) * mm});
            skLineSegment(sketch, "E136.MirrorCS", {"start": v(570, -300) * mm, "end": v(570, 0) * mm});
            skLineSegment(sketch, "E137.MirrorCS", {"start": v(600, -270) * mm, "end": v(0, -270) * mm});
            skLineSegment(sketch, "E138.MirrorCS", {"start": v(600, -300) * mm, "end": v(600, 0) * mm});
            skLineSegment(sketch, "E139.MirrorCS", {"start": v(600, -300) * mm, "end": v(0, -300) * mm});
            skLineSegment(sketch, "E140.MirrorCS", {"start": v(-570, -300) * mm, "end": v(-570, 0) * mm});
            skLineSegment(sketch, "E141.MirrorCS", {"start": v(-600, -270) * mm, "end": v(0, -270) * mm});
            skLineSegment(sketch, "E142.MirrorCS", {"start": v(-600, -300) * mm, "end": v(0, -300) * mm});
            skLineSegment(sketch, "E143.MirrorCS", {"start": v(-600, -300) * mm, "end": v(-600, 0) * mm});
            skCircle(sketch, "E144", {"center": v(-586, 286) * mm, "radius": 5 * mm});
            skCircle(sketch, "E145.MirrorC", {"center": v(586, 286) * mm, "radius": 5 * mm});
            skCircle(sketch, "E146.MirrorC", {"center": v(-586, -286) * mm, "radius": 5 * mm});
            skCircle(sketch, "E147.MirrorC", {"center": v(586, -286) * mm, "radius": 5 * mm});
            skSolve(sketch);
        }
        {
            var Q0;
            Q0=qCreatedBy(makeId("Front.planeOp"),FACE);
            var sketch = newSketch(context, id + "F6", { "sketchPlane" : qUnion([Q0])});
            skLineSegment(sketch, "E148.bottom", {"start": v(526.62, -156.75) * mm, "end": v(-539.74, -156.75) * mm});
            skLineSegment(sketch, "E148.top", {"start": v(526.62, 141.93) * mm, "end": v(-539.74, 141.93) * mm});
            skLineSegment(sketch, "E148.left", {"start": v(526.62, -156.75) * mm, "end": v(526.62, 141.93) * mm});
            skLineSegment(sketch, "E148.right", {"start": v(-539.74, -156.75) * mm, "end": v(-539.74, 141.93) * mm});
            skLineSegment(sketch, "E149.bottom", {"start": v(600, 170.75) * mm, "end": v(-600, 170.75) * mm});
            skLineSegment(sketch, "E149.top", {"start": v(600, 141.93) * mm, "end": v(-600, 141.93) * mm});
            skLineSegment(sketch, "E149.left", {"start": v(600, 170.75) * mm, "end": v(600, 141.93) * mm});
            skLineSegment(sketch, "E149.right", {"start": v(-600, 170.75) * mm, "end": v(-600, 141.93) * mm});
            skLineSegment(sketch, "E150.bottom", {"start": v(-505.68, 107.87) * mm, "end": v(500.42, 107.87) * mm});
            skLineSegment(sketch, "E150.top", {"start": v(-505.68, -127.93) * mm, "end": v(500.42, -127.93) * mm});
            skLineSegment(sketch, "E150.left", {"start": v(-505.68, 107.87) * mm, "end": v(-505.68, -127.93) * mm});
            skLineSegment(sketch, "E150.right", {"start": v(500.42, 107.87) * mm, "end": v(500.42, -127.93) * mm});
            skPoint(sketch, "E151.firstSnap0", {"position": v(-6.56, 141.93) * mm});
            skLineSegment(sketch, "E151.bottom", {"start": v(-6.56, 107.87) * mm, "end": v(26.2, 107.87) * mm});
            skLineSegment(sketch, "E151.top", {"start": v(-6.56, -127.93) * mm, "end": v(26.2, -127.93) * mm});
            skLineSegment(sketch, "E151.left", {"start": v(-6.56, 107.87) * mm, "end": v(-6.56, -127.93) * mm});
            skLineSegment(sketch, "E151.right", {"start": v(26.2, 107.87) * mm, "end": v(26.2, -127.93) * mm});
            skCircle(sketch, "E152", {"center": v(9.82, 130.43) * mm, "radius": 9.27 * mm});
            skPoint(sketch, "E152.centerSnap0", {"position": v(9.82, 107.87) * mm});
            skLineSegment(sketch, "E153.bottom", {"start": v(-472.12, 82.9) * mm, "end": v(-41.39, 82.9) * mm});
            skLineSegment(sketch, "E153.top", {"start": v(-472.12, -102.57) * mm, "end": v(-41.39, -102.57) * mm});
            skLineSegment(sketch, "E153.left", {"start": v(-472.12, 82.9) * mm, "end": v(-472.12, -102.57) * mm});
            skLineSegment(sketch, "E153.right", {"start": v(-41.39, 82.9) * mm, "end": v(-41.39, -102.57) * mm});
            skLineSegment(sketch, "E154.bottom", {"start": v(58.25, 78.3) * mm, "end": v(472.12, 78.3) * mm});
            skLineSegment(sketch, "E154.top", {"start": v(58.25, -102.57) * mm, "end": v(472.12, -102.57) * mm});
            skLineSegment(sketch, "E154.left", {"start": v(58.25, 78.3) * mm, "end": v(58.25, -102.57) * mm});
            skLineSegment(sketch, "E154.right", {"start": v(472.12, 78.3) * mm, "end": v(472.12, -102.57) * mm});
            skLineSegment(sketch, "E155", {"start": v(-539.74, 113.56) * mm, "end": v(-571.75, 141.93) * mm});
            skCircle(sketch, "E156", {"center": v(-505.68, -250.86) * mm, "radius": 79.3 * mm});
            skCircle(sketch, "E157", {"center": v(496.64, -247.32) * mm, "radius": 80.23 * mm});
            skPoint(sketch, "E158", {"position": v(-578.92, -144.72) * mm});
            skPoint(sketch, "E159", {"position": v(-448.01, -141.18) * mm});
            skPoint(sketch, "E160", {"position": v(500.42, -327.46) * mm});
            skPoint(sketch, "E161", {"position": v(496.64, -156.75) * mm});
            skCircle(sketch, "E162", {"center": v(-522.93, 130.55) * mm, "radius": 8.16 * mm});
            skSolve(sketch);
        }
        {
            var Q0;
            Q0=makeQuery(id+"F1.opExtrude","SWEPT_BODY",BODY,{"disambiguationData":[OSD([sQuery(id+"F0.wireOp",EDGE,"E0.bottom"),sQuery(id+"F0.wireOp",EDGE,"E0.top"),sQuery(id+"F0.wireOp",EDGE,"E0.left"),sQuery(id+"F0.wireOp",EDGE,"E1.top"),sQuery(id+"F0.wireOp",EDGE,"E5.MirrorCS"),sQuery(id+"F0.wireOp",EDGE,"E9.MirrorCS"),sQuery(id+"F0.wireOp",EDGE,"E10")])]});
            transform(context, id + "F7", {"entities" : qUnion([Q0]), "transformType" : TransformType.TRANSLATION_3D, "dx" : 0 * mm, "dy" : 0 * mm, "dz" : 0 * mm, "makeCopy" : true});
        }
        {
            var Q0;
            Q0=makeQuery(id+"F7.opPattern","COPY",BODY,{"derivedFrom":makeQuery(id+"F1.opExtrude","SWEPT_BODY",BODY,{"disambiguationData":[OSD([sQuery(id+"F0.wireOp",EDGE,"E0.bottom"),sQuery(id+"F0.wireOp",EDGE,"E0.top"),sQuery(id+"F0.wireOp",EDGE,"E0.left"),sQuery(id+"F0.wireOp",EDGE,"E1.top"),sQuery(id+"F0.wireOp",EDGE,"E5.MirrorCS"),sQuery(id+"F0.wireOp",EDGE,"E9.MirrorCS"),sQuery(id+"F0.wireOp",EDGE,"E10")])]}),"instanceName":"1"});
            deleteBodies(context, id + "F8", {"entities" : qUnion([Q0])});
        }
        {
            var Q0;
            Q0=makeQuery(id+"F0.imprint","IMPRINT",FACE,{"disambiguationData":[TD([[makeQuery(id+"F0.imprint","IMPRINT",EDGE,{"derivedFrom":sQuery(id+"F0.wireOp",EDGE,"E21.top")}),-1.0]])]});
            var Q1;
            {var subQ0=sQuery(id+"F0.wireOp",EDGE,"E24");Q1=makeQuery(id+"F0.imprint","IMPRINT",FACE,{"disambiguationData":[TD([[makeQuery(id+"F0.imprint","IMPRINT",EDGE,{"derivedFrom":subQ0}),1.0]])]});}
            var Q2;
            {var subQ1=sQuery(id+"F0.wireOp",EDGE,"E25");Q2=makeQuery(id+"F0.imprint","IMPRINT",FACE,{"disambiguationData":[TD([[makeQuery(id+"F0.imprint","IMPRINT",EDGE,{"derivedFrom":subQ1}),1.0]])]});}
            var Q3;
            {var subQ2=sQuery(id+"F0.wireOp",EDGE,"E29.MirrorCS");Q3=makeQuery(id+"F0.imprint","IMPRINT",FACE,{"disambiguationData":[TD([[makeQuery(id+"F0.imprint","IMPRINT",EDGE,{"derivedFrom":subQ2}),1.0]])]});}
            var Q4;
            {var subQ1=sQuery(id+"F0.wireOp",EDGE,"E57");Q4=makeQuery(id+"F0.imprint","IMPRINT",FACE,{"disambiguationData":[TD([[makeQuery(id+"F0.imprint","IMPRINT",EDGE,{"derivedFrom":subQ1}),1.0]])]});}
            var Q5;
            Q5=makeQuery(id+"F0.imprint","IMPRINT",FACE,{"disambiguationData":[TD([[makeQuery(id+"F0.imprint","IMPRINT",EDGE,{"derivedFrom":sQuery(id+"F0.wireOp",EDGE,"E54.bottom")}),1.0]])]});
            extrude(context, id + "F9", {"entities" : qUnion([Q0, Q1, Q2, Q3, Q4, Q5]), "operationType" : NewBodyOperationType.ADD, "depth" : 27 * mm});
        }
        {
            var Q0;
            {var subQ0=sQuery(id+"F0.wireOp",EDGE,"E31");var subQ1=sQuery(id+"F0.wireOp",EDGE,"E21.bottom");Q0=makeQuery(id+"F9.boolean.opBoolean","MERGE",FACE,{"derivedFrom":[makeQuery(id+"F2.opExtrude","SWEPT_FACE",FACE,{"disambiguationData":[OSD([subQ1,subQ0])]}),makeQuery(id+"F9.opExtrude","SWEPT_FACE",FACE,{"disambiguationData":[OSD([subQ1,subQ0])]})]});}
            var sketch = newSketch(context, id + "F10", { "sketchPlane" : qUnion([Q0])});
            skLineSegment(sketch, "E163", {"start": v(272.86, 0) * mm, "end": v(272.86, 27) * mm});
            skCircle(sketch, "E164", {"center": v(272.86, 14) * mm, "radius": 5 * mm});
            skLineSegment(sketch, "E165", {"start": v(-13.14, 0) * mm, "end": v(-13.14, 27) * mm});
            skLineSegment(sketch, "E166.MirrorCS", {"start": v(-299.14, 0) * mm, "end": v(-299.14, 27) * mm});
            skCircle(sketch, "E167.MirrorC", {"center": v(-299.14, 14) * mm, "radius": 5 * mm});
            skSolve(sketch);
        }
        {
            var Q0;
            Q0 = qSketchRegion(id + "F10", true);
            extrude(context, id + "F11", {"entities" : qUnion([Q0]), "operationType" : NewBodyOperationType.REMOVE, "endBound" : BoundingType.SYMMETRIC, "oppositeDirection" : true, "depth" : 30 * mm});
        }
        {
            var Q0;
            Q0 = qSketchRegion(id + "F5", true);
            var Q1;
            Q1=makeQuery(id+"F5.imprint","IMPRINT",FACE,{"disambiguationData":[TD([[makeQuery(id+"F5.imprint","IMPRINT",EDGE,{"derivedFrom":sQuery(id+"F5.wireOp",EDGE,"E107.top")}),-1.0]])]});
            extrude(context, id + "F12", {"entities" : qUnion([Q0, Q1]), "depth" : 2 * mm});
        }
        {
            var Q0;
            Q0=makeQuery(id+"F0.imprint","IMPRINT",FACE,{"disambiguationData":[TD([[makeQuery(id+"F0.imprint","IMPRINT",EDGE,{"derivedFrom":sQuery(id+"F0.wireOp",EDGE,"E44")}),1.0]])]});
            var Q1;
            Q1=makeQuery(id+"F0.imprint","IMPRINT",FACE,{"disambiguationData":[TD([[makeQuery(id+"F0.imprint","IMPRINT",EDGE,{"derivedFrom":sQuery(id+"F0.wireOp",EDGE,"E41.bottom")}),1.0]])]});
            var Q2;
            Q2=makeQuery(id+"F0.imprint","IMPRINT",FACE,{"disambiguationData":[TD([[makeQuery(id+"F0.imprint","IMPRINT",EDGE,{"derivedFrom":sQuery(id+"F0.wireOp",EDGE,"E86")}),1.0]])]});
            var Q3;
            {var subQ0=sQuery(id+"F0.wireOp",EDGE,"E86");Q3=makeQuery(id+"F0.imprint","IMPRINT",FACE,{"disambiguationData":[TD([[makeQuery(id+"F0.imprint","IMPRINT",EDGE,{"derivedFrom":subQ0}),-1.0]])]});}
            extrude(context, id + "F13", {"entities" : qUnion([Q0, Q1, Q2, Q3]), "operationType" : NewBodyOperationType.ADD, "depth" : 30 * mm});
        }
        {
            var Q0;
            {var subQ0=sQuery(id+"F0.wireOp",EDGE,"E48");var subQ1=sQuery(id+"F0.wireOp",EDGE,"E41.bottom");Q0=makeQuery(id+"F13.boolean.opBoolean","MERGE",FACE,{"derivedFrom":[makeQuery(id+"F2.opExtrude","SWEPT_FACE",FACE,{"disambiguationData":[OSD([subQ1,subQ0])]}),makeQuery(id+"F13.opExtrude","SWEPT_FACE",FACE,{"disambiguationData":[OSD([subQ1,subQ0])]})]});}
            var sketch = newSketch(context, id + "F14", { "sketchPlane" : qUnion([Q0])});
            skCircle(sketch, "E168", {"center": v(-144.74, 15) * mm, "radius": 5 * mm});
            skCircle(sketch, "E169", {"center": v(-381.7, 15) * mm, "radius": 5 * mm});
            skSolve(sketch);
        }
        {
            var Q0;
            Q0 = qSketchRegion(id + "F14", true);
            extrude(context, id + "F15", {"entities" : qUnion([Q0]), "operationType" : NewBodyOperationType.REMOVE, "endBound" : BoundingType.SYMMETRIC, "oppositeDirection" : true, "depth" : 30 * mm});
        }
        {
            var Q0;
            Q0=makeQuery(id+"F5.imprint","IMPRINT",FACE,{"disambiguationData":[TD([[makeQuery(id+"F5.imprint","IMPRINT",EDGE,{"derivedFrom":sQuery(id+"F5.wireOp",EDGE,"E107.top")}),-1.0]])]});
            var sketch = newSketch(context, id + "F16", { "sketchPlane" : qUnion([Q0])});
            skLineSegment(sketch, "E170.bottom", {"start": v(610, 310) * mm, "end": v(-610, 310) * mm});
            skLineSegment(sketch, "E170.top", {"start": v(610, -310) * mm, "end": v(-610, -310) * mm});
            skLineSegment(sketch, "E170.left", {"start": v(610, 310) * mm, "end": v(610, -310) * mm});
            skLineSegment(sketch, "E170.right", {"start": v(-610, 310) * mm, "end": v(-610, -310) * mm});
            skSolve(sketch);
        }
        {
            var Q0;
            Q0 = qSketchRegion(id + "F16", true);
            extrude(context, id + "F17", {"entities" : qUnion([Q0]), "depth" : 30 * mm});
        }
        {
            var Q0;
            {var subQ0=sQuery(id+"F0.wireOp",EDGE,"E83.bottom");Q0=makeQuery(id+"F13.boolean.opBoolean","MERGE",FACE,{"derivedFrom":[makeQuery(id+"F2.opExtrude","SWEPT_FACE",FACE,{"disambiguationData":[OSD([subQ0])]}),makeQuery(id+"F13.opExtrude","SWEPT_FACE",FACE,{"disambiguationData":[OSD([subQ0])]})]});}
            var sketch = newSketch(context, id + "F18", { "sketchPlane" : qUnion([Q0])});
            skCircle(sketch, "E171", {"center": v(-107.42, 15) * mm, "radius": 5 * mm});
            skCircle(sketch, "E172", {"center": v(-344.4, 15) * mm, "radius": 5 * mm});
            skPoint(sketch, "E172.centerSnap0", {"position": v(-242.4, 15) * mm});
            skSolve(sketch);
        }
        {
            var Q0;
            Q0 = qSketchRegion(id + "F18", true);
            extrude(context, id + "F19", {"entities" : qUnion([Q0]), "operationType" : NewBodyOperationType.REMOVE, "oppositeDirection" : true, "depth" : 25 * mm});
        }
    });
